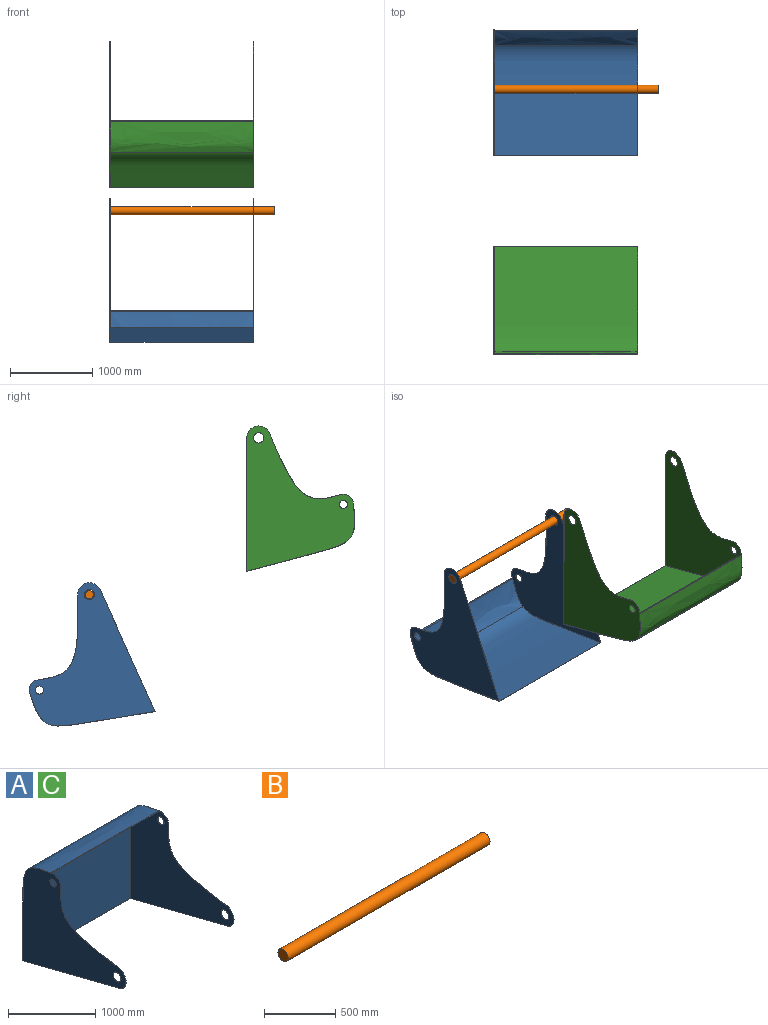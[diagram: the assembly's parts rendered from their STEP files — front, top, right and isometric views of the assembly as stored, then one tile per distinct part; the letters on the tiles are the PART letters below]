
ASSEMBLY  parts=3 mates=2
PART A: 20 faces, bbox 1750x1685x1465 mm
  f0: plane 1750x1575.63mm, normal (0,-0.25,-0.97), area 12639.7mm2, adj f3,f8,f9,f13,f14,f16,f18,f19
  f1: extruded ~913.85x647.45mm, area 3226.6mm2, adj f3,f5,f14,f19
  f2: cylinder r=50mm len=100mm, axis (-1,0,0), area 785.4mm2, adj f14,f19
  f3: cylinder r=145mm len=285.55mm, axis (-1,0,0), area 1048.8mm2, adj f0,f1,f14,f19
  f4: cylinder r=62.5mm len=125mm, axis (-1,0,0), area 981.7mm2, adj f14,f19
  f5: cylinder r=125mm len=154.71mm, axis (-1,0,0), area 584.8mm2, adj f1,f11,f14,f19
  f6: cylinder r=125mm len=154.71mm, axis (-1,0,0), area 584.8mm2, adj f7,f11,f13,f18
  f7: extruded ~913.85x647.45mm, area 3226.6mm2, adj f6,f8,f13,f18
  f8: cylinder r=145mm len=285.55mm, axis (-1,0,0), area 1048.8mm2, adj f0,f7,f13,f18
  f9: extruded ~1750x1340mm, area 2378956.1mm2, adj f0,f11,f13,f14
  f10: cylinder r=62.5mm len=125mm, axis (-1,0,0), area 981.7mm2, adj f13,f18
  f11: extruded ~1750x370.29mm, area 693414.2mm2, adj f5,f6,f9,f13,f14,f15
  f12: cylinder r=50mm len=100mm, axis (-1,0,0), area 785.4mm2, adj f13,f18
  f13: plane 1685x1465mm, normal (1,0,0), area 1305753.8mm2, adj f0,f6,f7,f8,f9,f10,f11,f12
  f14: plane 1685x1465mm, normal (-1,0,0), area 1305753.8mm2, adj f0,f1,f2,f3,f4,f5,f9,f11
  f15: cylinder r=125mm len=1745mm, axis (-1,0,0), area 26474mm2, adj f11,f17,f18,f19
  f16: extruded ~1745x1337.61mm, area 2367662mm2, adj f0,f17,f18,f19
  f17: extruded ~1745x354.02mm, area 662459.2mm2, adj f15,f16,f18,f19
  f18: plane 1682.49x1464.36mm, normal (-1,0,0), area 1301505mm2, adj f0,f6,f7,f8,f10,f12,f15,f16
  f19: plane 1682.49x1464.36mm, normal (1,0,0), area 1301505mm2, adj f0,f1,f2,f3,f4,f5,f15,f16
PART B: 3 faces, bbox 2000x100x100 mm
  f0: cylinder r=50mm len=2000mm, axis (-1,0,0), area 628318.5mm2, adj f1,f2
  f1: plane 100x100mm, normal (1,0,0), area 7854mm2, adj f0
  f2: plane 100x100mm, normal (-1,0,0), area 7854mm2, adj f0
PART C: same geometry as A
PLACE A rot(axis=(-1,0,0),100deg) t=(-1277.9,-2394.35,1272.55)mm
PLACE B rot(axis=(0,-0.64,0.77),180deg) t=(722.1,-1698.05,2111.76)mm
PLACE C rot(axis=(0,-0.61,0.79),180deg) t=(472.1,-3466.44,2968.36)mm
MATE cylindrical A.f3 <-> B.f0  axis (-1,0,0) through (-1277.9,-1698.05,2111.76)mm
MATE planar C.f3 <-> A.f3  axis (1,0,0) through (472.1,-3757.64,4019.22)mm
